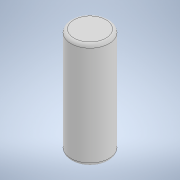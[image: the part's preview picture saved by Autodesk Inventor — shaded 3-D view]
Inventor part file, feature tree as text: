
AUTODESK INVENTOR PART (.ipt)
format: ipt  version: 2021 (Build 250183000, 183)  size: 108,544 bytes
history: native  units: mm
features: fillet x2, extrude x1, sketch x1
ambient origin geometry x8: Origin, YZ Plane, XZ Plane, XY Plane, X Axis, Y Axis, Z Axis, Center Point
bodies: Body1 (feature_tree)
feature tree (4):
  extrude  "Extrusion2"  Depth=16.6mm TaperAngle=0.0deg
  fillet  "Fillet1"  Radius=0.5mm
  fillet  "Fillet2"  Radius=0.5mm
  sketch  "Sketch1"  dims[d0=6.0mm d3=16.6mm d4=0.0mm d5=0.5mm d6=0.5mm]
